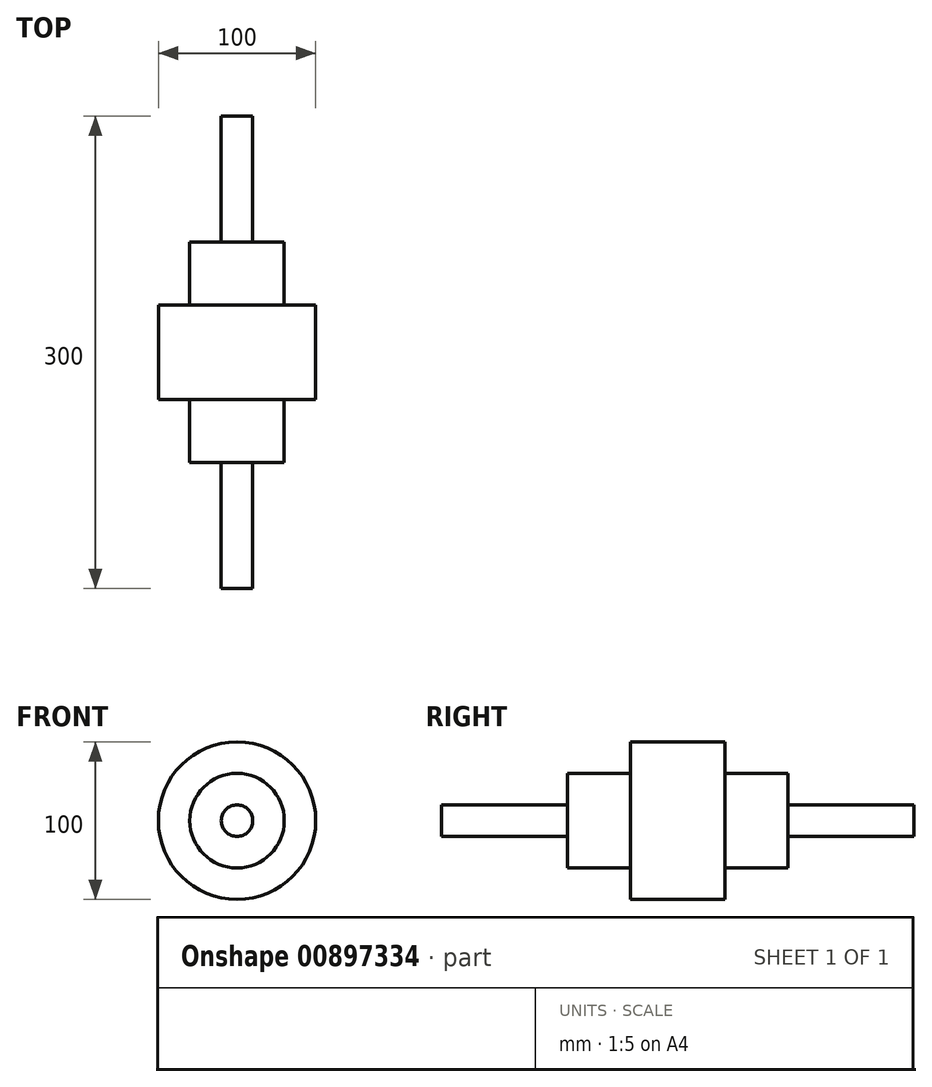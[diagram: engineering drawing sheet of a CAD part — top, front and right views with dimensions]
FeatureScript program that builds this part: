
annotation { "Feature Type Name" : "Feature", "Feature Type Description" : "" }
export const myFeature = defineFeature(function(context is Context, id is Id, definition is map)
    precondition{}
    {
        {
            var Q0;
            Q0=qCreatedBy(makeId("Front.planeOp"),FACE);
            var sketch = newSketch(context, id + "F0", { "sketchPlane" : qUnion([Q0])});
            skCircle(sketch, "E0", {"center": v(0, 0) * mm, "radius": 50 * mm});
            skSolve(sketch);
        }
        {
            var Q0;
            Q0=makeQuery(id+"F0.imprint","IMPRINT",FACE,{"disambiguationData":[TD([[makeQuery(id+"F0.imprint","IMPRINT",EDGE,{"derivedFrom":sQuery(id+"F0.wireOp",EDGE,"E0")}),1.0]])]});
            extrude(context, id + "F1", {"entities" : qUnion([Q0]), "depth" : 60 * mm, "offsetDistance" : 25.4 * mm});
        }
        {
            var Q0;
            Q0=makeQuery(id+"F1.opExtrude","CAP_FACE",FACE,{"disambiguationData":[OSD([sQuery(id+"F0.wireOp",EDGE,"E0")])],"isStart":false});
            var sketch = newSketch(context, id + "F2", { "sketchPlane" : qUnion([Q0])});
            skCircle(sketch, "E1", {"center": v(0, 0) * mm, "radius": 30 * mm});
            skSolve(sketch);
        }
        {
            var Q0;
            Q0=makeQuery(id+"F2.imprint","IMPRINT",FACE,{"disambiguationData":[TD([[makeQuery(id+"F2.imprint","IMPRINT",EDGE,{"derivedFrom":sQuery(id+"F2.wireOp",EDGE,"E1")}),1.0]])]});
            extrude(context, id + "F3", {"entities" : qUnion([Q0]), "operationType" : NewBodyOperationType.ADD, "depth" : 40 * mm, "offsetDistance" : 25.4 * mm});
        }
        {
            var Q0;
            Q0=makeQuery(id+"F3.opExtrude","CAP_FACE",FACE,{"disambiguationData":[OSD([sQuery(id+"F2.wireOp",EDGE,"E1")])],"isStart":false});
            var sketch = newSketch(context, id + "F4", { "sketchPlane" : qUnion([Q0])});
            skCircle(sketch, "E2", {"center": v(0, 0) * mm, "radius": 10 * mm});
            skSolve(sketch);
        }
        {
            var Q0;
            Q0=makeQuery(id+"F4.imprint","IMPRINT",FACE,{"disambiguationData":[TD([[makeQuery(id+"F4.imprint","IMPRINT",EDGE,{"derivedFrom":sQuery(id+"F4.wireOp",EDGE,"E2")}),1.0]])]});
            extrude(context, id + "F5", {"entities" : qUnion([Q0]), "operationType" : NewBodyOperationType.ADD, "depth" : 80 * mm, "offsetDistance" : 25.4 * mm});
        }
        {
            var Q0;
            Q0=makeQuery(id+"F1.opExtrude","CAP_FACE",FACE,{"disambiguationData":[OSD([sQuery(id+"F0.wireOp",EDGE,"E0")])],"isStart":true});
            var sketch = newSketch(context, id + "F6", { "sketchPlane" : qUnion([Q0])});
            skCircle(sketch, "E3", {"center": v(0, 0) * mm, "radius": 30 * mm});
            skSolve(sketch);
        }
        {
            var Q0;
            Q0=makeQuery(id+"F6.imprint","IMPRINT",FACE,{"disambiguationData":[TD([[makeQuery(id+"F6.imprint","IMPRINT",EDGE,{"derivedFrom":sQuery(id+"F6.wireOp",EDGE,"E3")}),1.0]])]});
            extrude(context, id + "F7", {"entities" : qUnion([Q0]), "operationType" : NewBodyOperationType.ADD, "depth" : 40 * mm, "offsetDistance" : 25.4 * mm});
        }
        {
            var Q0;
            Q0=makeQuery(id+"F7.opExtrude","CAP_FACE",FACE,{"disambiguationData":[OSD([sQuery(id+"F6.wireOp",EDGE,"E3")])],"isStart":false});
            var sketch = newSketch(context, id + "F8", { "sketchPlane" : qUnion([Q0])});
            skCircle(sketch, "E4", {"center": v(0, 0) * mm, "radius": 10 * mm});
            skSolve(sketch);
        }
        {
            var Q0;
            Q0=makeQuery(id+"F8.imprint","IMPRINT",FACE,{"disambiguationData":[TD([[makeQuery(id+"F8.imprint","IMPRINT",EDGE,{"derivedFrom":sQuery(id+"F8.wireOp",EDGE,"E4")}),1.0]])]});
            extrude(context, id + "F9", {"entities" : qUnion([Q0]), "operationType" : NewBodyOperationType.ADD, "depth" : 80 * mm, "offsetDistance" : 25.4 * mm});
        }
    });
